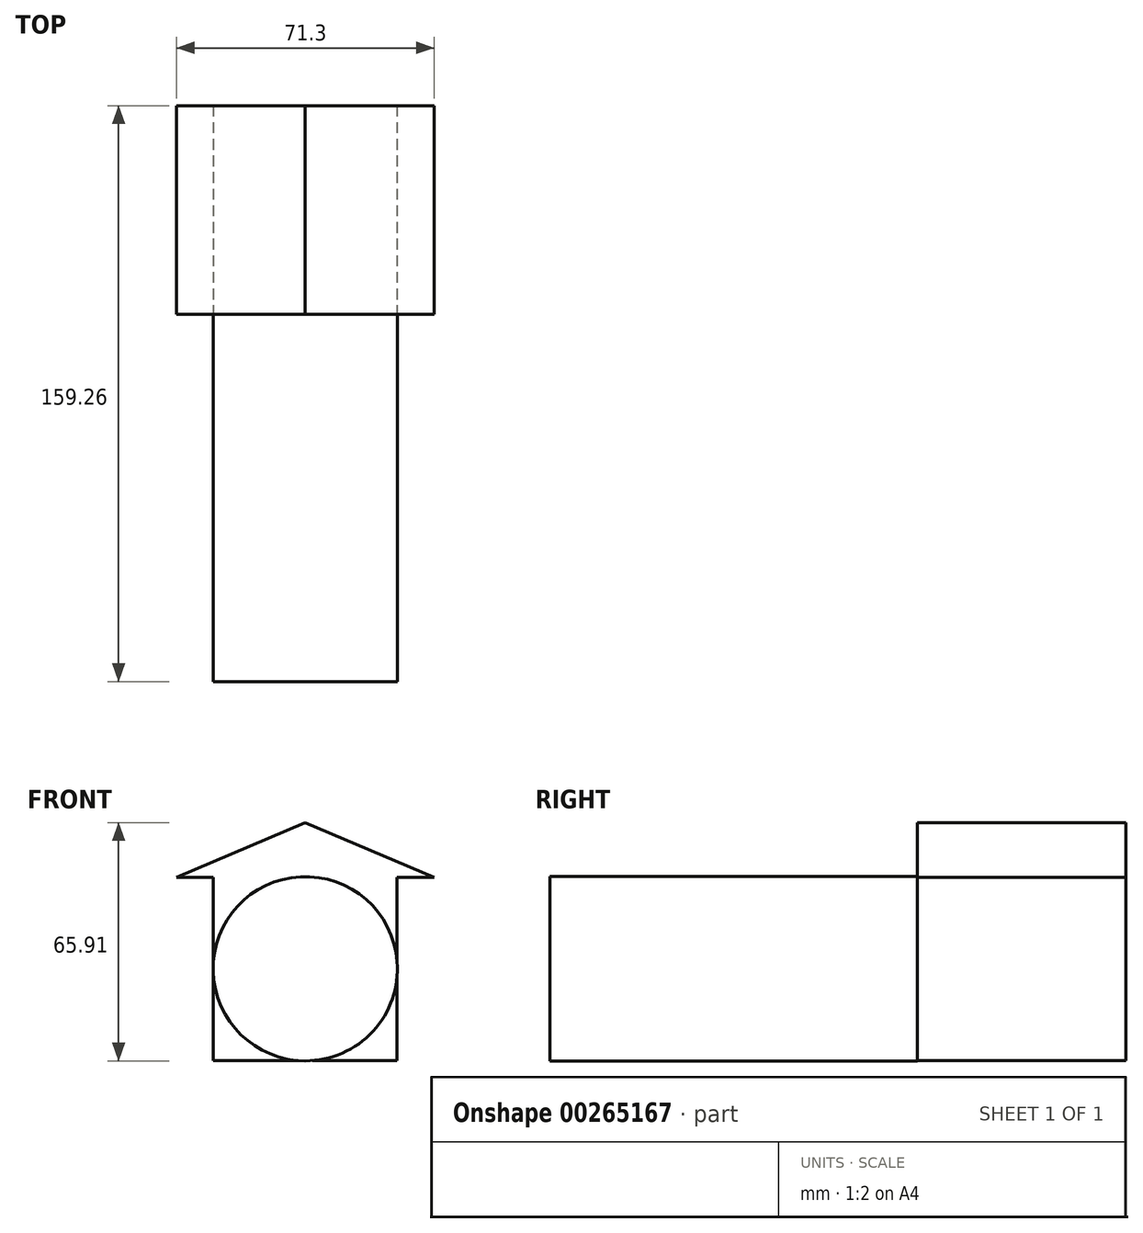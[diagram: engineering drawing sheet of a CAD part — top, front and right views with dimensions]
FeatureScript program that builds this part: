
annotation { "Feature Type Name" : "Feature", "Feature Type Description" : "" }
export const myFeature = defineFeature(function(context is Context, id is Id, definition is map)
    precondition{}
    {
        {
            var Q0;
            Q0=qCreatedBy(makeId("Front.planeOp"),FACE);
            var sketch = newSketch(context, id + "F0", { "sketchPlane" : qUnion([Q0])});
            skCircle(sketch, "E0", {"center": v(0, 0) * mm, "radius": 25.48 * mm});
            skSolve(sketch);
        }
        {
            var Q0;
            Q0=makeQuery(id+"F0.imprint","IMPRINT",FACE,{"disambiguationData":[TD([[makeQuery(id+"F0.imprint","IMPRINT",EDGE,{"derivedFrom":sQuery(id+"F0.wireOp",EDGE,"E0")}),1.0]])]});
            extrude(context, id + "F1", {"entities" : qUnion([Q0]), "depth" : 101.6 * mm});
        }
        {
            var Q0;
            Q0=qCreatedBy(makeId("Top.planeOp"),FACE);
            var sketch = newSketch(context, id + "F2", { "sketchPlane" : qUnion([Q0])});
            skCircle(sketch, "E1", {"center": v(0, -66.09) * mm, "radius": 14.8 * mm});
            skSolve(sketch);
        }
        {
            var Q0;
            Q0=qCreatedBy(makeId("Front.planeOp"),FACE);
            var sketch = newSketch(context, id + "F3", { "sketchPlane" : qUnion([Q0])});
            skLineSegment(sketch, "E2.bottom", {"start": v(-25.4, -25.4) * mm, "end": v(25.4, -25.4) * mm});
            skLineSegment(sketch, "E2.top", {"start": v(-25.4, 25.4) * mm, "end": v(25.4, 25.4) * mm});
            skLineSegment(sketch, "E2.left", {"start": v(-25.4, -25.4) * mm, "end": v(-25.4, 25.4) * mm});
            skLineSegment(sketch, "E2.right", {"start": v(25.4, -25.4) * mm, "end": v(25.4, 25.4) * mm});
            skPoint(sketch, "E2.middle", {"position": v(0, 0) * mm});
            skSolve(sketch);
        }
        {
            var Q0;
            Q0=makeQuery(id+"F3.imprint","IMPRINT",FACE,{"disambiguationData":[TD([[makeQuery(id+"F3.imprint","IMPRINT",EDGE,{"derivedFrom":sQuery(id+"F3.wireOp",EDGE,"E2.bottom")}),1.0]])]});
            extrude(context, id + "F4", {"entities" : qUnion([Q0]), "operationType" : NewBodyOperationType.ADD, "oppositeDirection" : true, "depth" : 57.66 * mm});
        }
        {
            var Q0;
            Q0=qCreatedBy(makeId("Front.planeOp"),FACE);
            var sketch = newSketch(context, id + "F5", { "sketchPlane" : qUnion([Q0])});
            skLineSegment(sketch, "E3", {"start": v(0, 40.43) * mm, "end": v(35.65, 25.27) * mm});
            skLineSegment(sketch, "E4", {"start": v(35.65, 25.27) * mm, "end": v(-35.65, 25.27) * mm});
            skLineSegment(sketch, "E5", {"start": v(-35.65, 25.27) * mm, "end": v(0, 40.43) * mm});
            skSolve(sketch);
        }
        {
            var Q0;
            Q0=makeQuery(id+"F5.imprint","IMPRINT",FACE,{"disambiguationData":[TD([[makeQuery(id+"F5.imprint","IMPRINT",EDGE,{"derivedFrom":sQuery(id+"F5.wireOp",EDGE,"E3")}),-1.0]])]});
            extrude(context, id + "F6", {"entities" : qUnion([Q0]), "operationType" : NewBodyOperationType.ADD, "oppositeDirection" : true, "depth" : 57.66 * mm});
        }
        {
            var Q0;
            Q0=sQuery(id+"F2.wireOp",EDGE,"E1");
            extrude(context, id + "F7", {"bodyType" : ToolBodyType.SURFACE, "surfaceEntities" : qUnion([Q0]), "depth" : 51.05 * mm});
        }
    });
